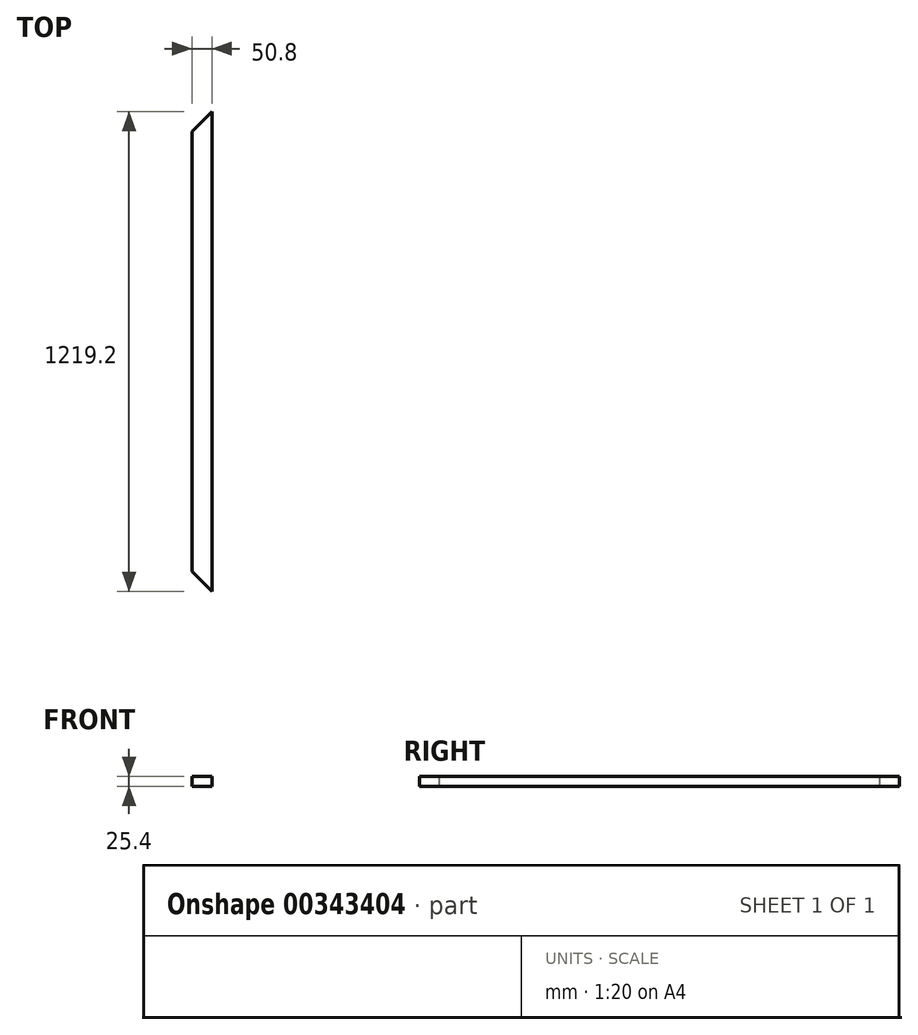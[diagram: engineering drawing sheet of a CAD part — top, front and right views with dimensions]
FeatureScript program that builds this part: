
annotation { "Feature Type Name" : "Feature", "Feature Type Description" : "" }
export const myFeature = defineFeature(function(context is Context, id is Id, definition is map)
    precondition{}
    {
        {
            var Q0;
            Q0=qCreatedBy(makeId("Front.planeOp"),FACE);
            var sketch = newSketch(context, id + "F0", { "sketchPlane" : qUnion([Q0])});
            skLineSegment(sketch, "E0.bottom", {"start": v(-14.3, 31.27) * mm, "end": v(-65.1, 31.27) * mm});
            skLineSegment(sketch, "E0.top", {"start": v(-14.3, 56.67) * mm, "end": v(-65.1, 56.67) * mm});
            skLineSegment(sketch, "E0.left", {"start": v(-14.3, 31.27) * mm, "end": v(-14.3, 56.67) * mm});
            skLineSegment(sketch, "E0.right", {"start": v(-65.1, 31.27) * mm, "end": v(-65.1, 56.67) * mm});
            skPoint(sketch, "E0.middle", {"position": v(-39.7, 43.97) * mm});
            skSolve(sketch);
        }
        {
            var Q0;
            Q0 = qSketchRegion(id + "F0", true);
            extrude(context, id + "F1", {"entities" : qUnion([Q0]), "depth" : 1219.2 * mm});
        }
        {
            var Q0;
            Q0=makeQuery(id+"F1.opExtrude","CAP_EDGE",EDGE,{"disambiguationData":[OSD([sQuery(id+"F0.wireOp",EDGE,"E0.right")])],"isStart":true});
            chamfer(context, id + "F2", {"entities" : qUnion([Q0]), "width" : 50.8 * mm, "tangentPropagation" : true});
        }
        {
            var Q0;
            Q0=makeQuery(id+"F1.opExtrude","CAP_EDGE",EDGE,{"disambiguationData":[OSD([sQuery(id+"F0.wireOp",EDGE,"E0.right")])],"isStart":false});
            chamfer(context, id + "F3", {"entities" : qUnion([Q0]), "width" : 50.8 * mm, "tangentPropagation" : true});
        }
    });
